# Revit family: BE_84764_de_DE
name_source: partatom
category: Leuchten
units: mm (PartAtom-declared; Revit-internal decimal feet)

## family parameters
Basisbauteil = Fläche
Beim Laden mit Abzugskörper schneiden = Ja
Bemaßung runder Anschluss = Durchmesser verwenden
Gemeinsam genutzt = Nein
Lichtquelle = Nein
Raumberechnungspunkt = Ja
Teiletyp = Normal

## types (3) — shared parameters
AC/DC = AC/DC
Aktualisierung = 2022-05-19T04:00:07
BEGA_Dummy = Nein
BEGA_Intern = Ja
BEGA_Intern_Konstruktion = Ja
BEGA_Intern_an = Ja
BEGA_Intern_aus = Ja
Befestigungsabstand = 85 mm
Befestigungsbohrung = Ø 5,5 mm
Beschreibung = Hochleistungsscheinwerfer
Beschreibung_Sonderanfertigung = Hier können Sie Informationen zur Sonderanfertigung eintragen.
CE_Konformität = ja
ENEC = ja
Energieeffizienzklasse = LED A++ - A
Frequenz = 0/50-60 Hz
Gewicht = 17.15 kg
Hersteller = BEGA
Lampe = LED 170.4 W
Lastklassifizierung = Beleuchtung
Lebensdauerkriterien = L70B50 @ 25 °C = 130000 h
Logo = BEGA_Logo.png
M_A = Nein
M_G = Ja
M_W = Nein
Material_06 = BEGA_Oberfläche_Edelstahl_gebürstet
Material_09 = BEGA_Glas_klar
Material_15 = BEGA_Leuchtmedium_matt
Material_17 = BEGA_Reflektor
Material_18 = BEGA_Gummi_schwarz
Produktdatenblatt = https://cdn.bega.com
Scheinlast = 0 VA
Schutzart = IP 67
Schutzklasse = I
Sonderanfertigung = Nein
Spannung = 240 V
Typenbild = 84206.png
URL = https://www.bega.com
Umgebungstemperatur = 25 °C
zero-valued in all types: Vorgabe-Ansicht

## per-type parameters (varying)
| type | BEGA_IES1 | BEGA_IES2 | BEGA_IES3 | Bestellnummer | Farbtemperatur | Farbwiedergabeindex | LED_Modulbezeichnung | Lampenlichtstrom | Leuchtenlichtstrom | Modell |
| BEGA_84764_Grafit_K3 | Nein | Ja | Nein | 84764K3 | 3000 K | CRI > 80 | 4x LED-0705/830 | 25980 lm | 17353 lm | 84764K3 |
| BEGA_84764_Grafit_K4 | Nein | Nein | Ja | 84764K4 | 4000 K | CRI > 80 | 4x LED-0705/840 | 26660 lm | 17807 lm | 84764K4 |
| BEGA_84764_Grafit_K22 | Ja | Ja | Ja | 84764K22 | 2200 K | CRI > 65 | 4x LED-0705/622 | 25020 lm | 16712 lm | 84764K22 |

## geometry (parser evidence)
native form markers: Sweep x16
no freeform markers — native parametric forms only
